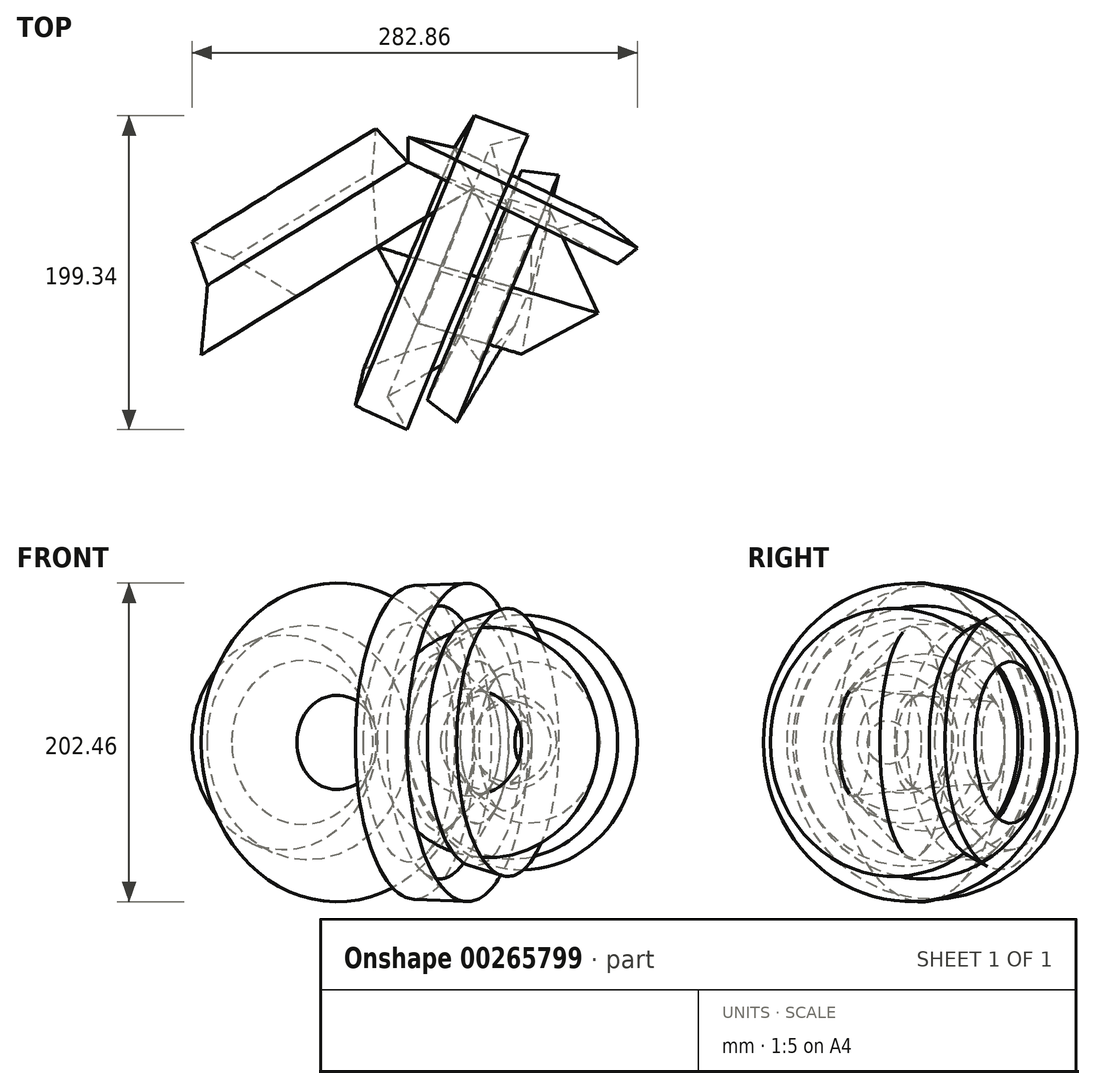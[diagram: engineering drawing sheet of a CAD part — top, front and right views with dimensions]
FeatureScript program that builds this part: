
annotation { "Feature Type Name" : "Feature", "Feature Type Description" : "" }
export const myFeature = defineFeature(function(context is Context, id is Id, definition is map)
    precondition{}
    {
        {
            var Q0;
            Q0=qCreatedBy(makeId("Top.planeOp"),FACE);
            var sketch = newSketch(context, id + "F0", { "sketchPlane" : qUnion([Q0])});
            skLineSegment(sketch, "E0", {"start": v(-43.5, 36.63) * mm, "end": v(-40.45, -10.99) * mm});
            skLineSegment(sketch, "E1", {"start": v(-40.45, -10.99) * mm, "end": v(20.3, 26.25) * mm});
            skLineSegment(sketch, "E2", {"start": v(20.3, 26.25) * mm, "end": v(0, -26.56) * mm});
            skLineSegment(sketch, "E3", {"start": v(0, -26.56) * mm, "end": v(-14.2, -59.53) * mm});
            skLineSegment(sketch, "E4", {"start": v(-14.2, -59.53) * mm, "end": v(36.17, -59.53) * mm});
            skLineSegment(sketch, "E5", {"start": v(36.17, -59.53) * mm, "end": v(42.9, -33.58) * mm});
            skLineSegment(sketch, "E6", {"start": v(42.9, -33.58) * mm, "end": v(23.05, -36.02) * mm});
            skLineSegment(sketch, "E7", {"start": v(23.05, -36.02) * mm, "end": v(37.4, -6.41) * mm});
            skLineSegment(sketch, "E8", {"start": v(37.4, -6.41) * mm, "end": v(57.54, -3.05) * mm});
            skLineSegment(sketch, "E9", {"start": v(57.54, -3.05) * mm, "end": v(57.54, -35.1) * mm});
            skLineSegment(sketch, "E10", {"start": v(57.54, -35.1) * mm, "end": v(74.64, 34.8) * mm});
            skLineSegment(sketch, "E11", {"start": v(74.64, 34.8) * mm, "end": v(51.13, 37.55) * mm});
            skLineSegment(sketch, "E12", {"start": v(51.13, 37.55) * mm, "end": v(42.9, 11.9) * mm});
            skLineSegment(sketch, "E13", {"start": v(42.9, 11.9) * mm, "end": v(31.9, 54.03) * mm});
            skLineSegment(sketch, "E14", {"start": v(31.9, 54.03) * mm, "end": v(55.18, 60.1) * mm});
            skLineSegment(sketch, "E15", {"start": v(55.18, 60.1) * mm, "end": v(21.22, 72.35) * mm});
            skLineSegment(sketch, "E16", {"start": v(21.22, 72.35) * mm, "end": v(8.7, 52.2) * mm});
            skLineSegment(sketch, "E17", {"start": v(8.7, 52.2) * mm, "end": v(-20.91, 58.92) * mm});
            skLineSegment(sketch, "E18", {"start": v(-20.91, 58.92) * mm, "end": v(-20.91, 42.74) * mm});
            skLineSegment(sketch, "E19", {"start": v(-20.91, 42.74) * mm, "end": v(-41.36, 64.1) * mm});
            skLineSegment(sketch, "E20", {"start": v(-41.36, 64.1) * mm, "end": v(-43.5, 36.63) * mm});
            skLineSegment(sketch, "E21", {"start": v(-20.91, 42.74) * mm, "end": v(20.3, 26.25) * mm});
            skLineSegment(sketch, "E22", {"start": v(42.9, 11.9) * mm, "end": v(37.4, -6.41) * mm});
            skLineSegment(sketch, "E23", {"start": v(0, -26.56) * mm, "end": v(23.05, -36.02) * mm});
            skLineSegment(sketch, "E24", {"start": v(20.3, 26.25) * mm, "end": v(8.7, 52.2) * mm});
            skLineSegment(sketch, "E25", {"start": v(20.3, 26.25) * mm, "end": v(37.4, -6.41) * mm});
            skLineSegment(sketch, "E26", {"start": v(-40.45, -10.99) * mm, "end": v(-14.2, -59.53) * mm});
            skLineSegment(sketch, "E27", {"start": v(-70.36, -19.54) * mm, "end": v(-52.3, -49) * mm});
            skSolve(sketch);
        }
        {
            var Q0;
            Q0=makeQuery(id+"F0.imprint","IMPRINT",FACE,{"disambiguationData":[TD([[makeQuery(id+"F0.imprint","IMPRINT",EDGE,{"derivedFrom":sQuery(id+"F0.wireOp",EDGE,"E0")}),1.0]])]});
            var Q1;
            Q1=sQuery(id+"F0.wireOp",EDGE,"E27");
            revolve(context, id + "F1", {"entities" : qUnion([Q0]), "axis" : qUnion([Q1]), "revolveType" : RevolveType.FULL});
        }
        {
            var Q0;
            Q0=makeQuery(id+"F0.imprint","IMPRINT",FACE,{"disambiguationData":[TD([[makeQuery(id+"F0.imprint","IMPRINT",EDGE,{"derivedFrom":sQuery(id+"F0.wireOp",EDGE,"E17")}),1.0]])]});
            var Q1;
            Q1=sQuery(id+"F0.wireOp",EDGE,"E7");
            revolve(context, id + "F2", {"entities" : qUnion([Q0]), "axis" : qUnion([Q1]), "revolveType" : RevolveType.FULL});
        }
        {
            var Q0;
            Q0=makeQuery(id+"F0.imprint","IMPRINT",FACE,{"disambiguationData":[TD([[makeQuery(id+"F0.imprint","IMPRINT",EDGE,{"derivedFrom":sQuery(id+"F0.wireOp",EDGE,"E13")}),1.0]])]});
            var Q1;
            Q1=sQuery(id+"F0.wireOp",EDGE,"E23");
            revolve(context, id + "F3", {"entities" : qUnion([Q0]), "axis" : qUnion([Q1]), "revolveType" : RevolveType.FULL});
        }
        {
            var Q0;
            Q0=makeQuery(id+"F0.imprint","IMPRINT",FACE,{"disambiguationData":[TD([[makeQuery(id+"F0.imprint","IMPRINT",EDGE,{"derivedFrom":sQuery(id+"F0.wireOp",EDGE,"E1")}),-1.0]])]});
            var Q1;
            Q1=sQuery(id+"F0.wireOp",EDGE,"E22");
            revolve(context, id + "F4", {"entities" : qUnion([Q0]), "axis" : qUnion([Q1]), "revolveType" : RevolveType.FULL});
        }
        {
            var Q0;
            Q0=makeQuery(id+"F0.imprint","IMPRINT",FACE,{"disambiguationData":[TD([[makeQuery(id+"F0.imprint","IMPRINT",EDGE,{"derivedFrom":sQuery(id+"F0.wireOp",EDGE,"E8")}),1.0]])]});
            var Q1;
            Q1=sQuery(id+"F0.wireOp",EDGE,"E23");
            revolve(context, id + "F5", {"entities" : qUnion([Q0]), "axis" : qUnion([Q1]), "revolveType" : RevolveType.FULL});
        }
    });
